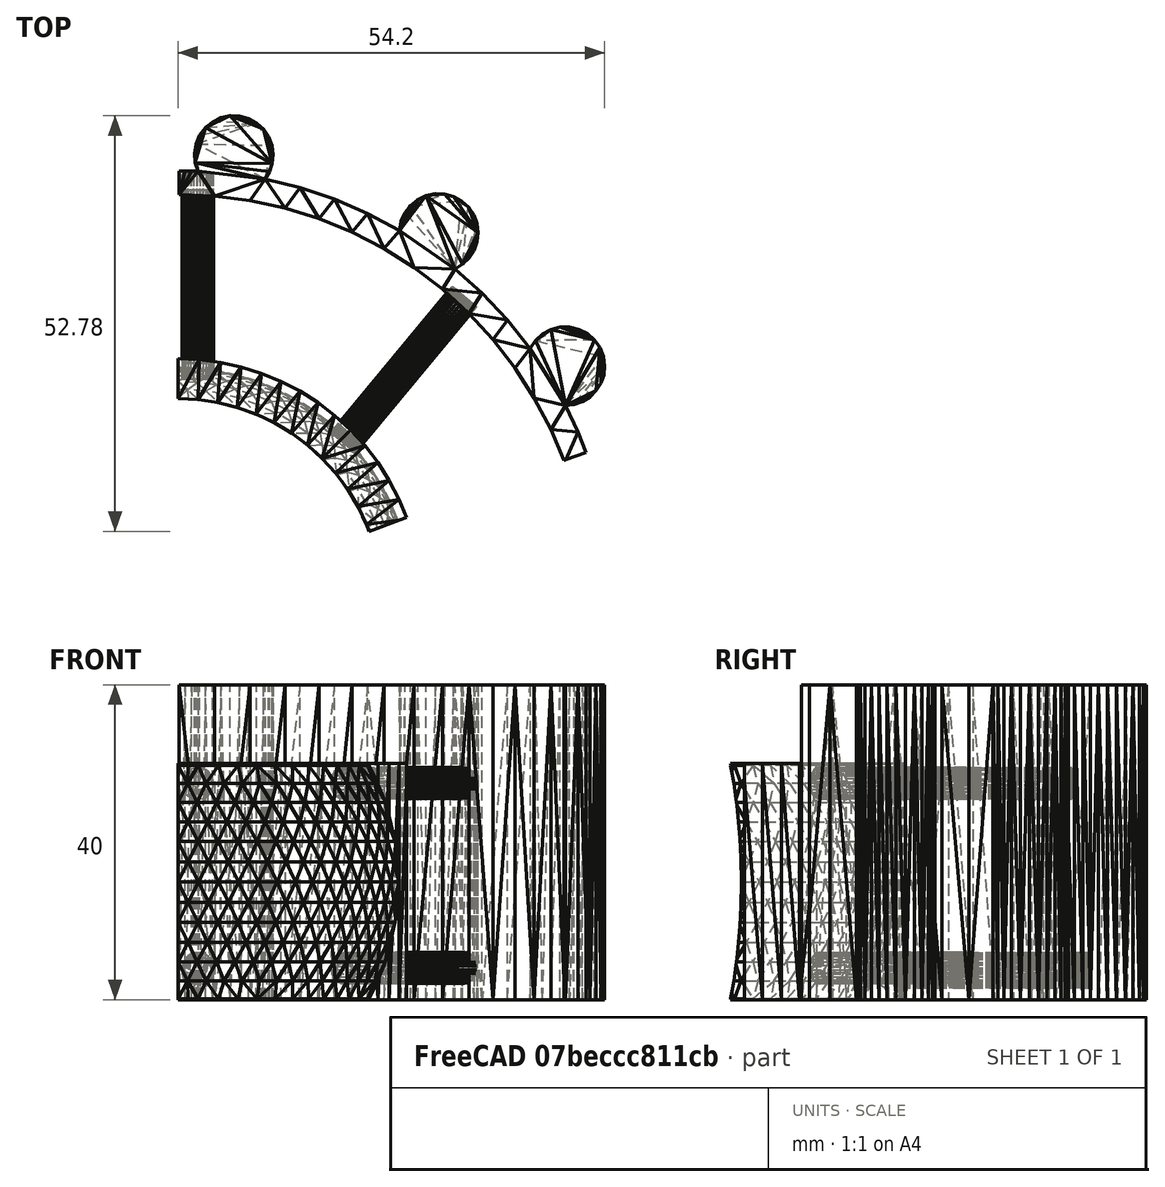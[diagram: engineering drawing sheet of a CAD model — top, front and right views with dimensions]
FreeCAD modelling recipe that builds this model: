
FCSTD DOCUMENT  (FreeCAD 1.1R43946 (Git))
Label: solid_door_handle_arthritis
License: All rights reserved
LicenseURL: https://en.wikipedia.org/wiki/All_rights_reserved
objects: Part::Box×3, Part::Cut×3, Mesh::Feature×1, Part::Feature×1
note: 7 computed .brp shape members not serialized (recipe doc carries the construction recipe); baked Part::Feature solids carry a one-line shape summary decoded from their .brp

FEATURE [Mesh::Feature] arthritis_door_handle_mk3
FEATURE [Part::Feature] arthritis_door_handle_mk001
  shape: bbox 64.29 x 63.81 x 40 mm, 1954 faces, 0 solids (baked)
FEATURE [Part::Box] Box  label="Cube"
  AttacherType = Attacher::AttachEngine3D
  Height = 100
  Length = 101
  Placement = pos=(0,-20,0) rot=(0,0,1;0.349066rad)
  Width = 19
FEATURE [Part::Cut] Cut
  Base = -> arthritis_door_handle_mk001
  Refine = true
  Tool = -> Box
FEATURE [Part::Box] Box001  label="Cube001"
  AttacherType = Attacher::AttachEngine3D
  Height = 45
  Length = 10
  Placement = pos=(-4,-3.5,0) rot=(0,0,1;0rad)
  Width = 10
FEATURE [Part::Cut] Cut001
  Base = -> Cut
  Refine = true
  Tool = -> Box001
FEATURE [Part::Box] Box002  label="Cube002"
  AttacherType = Attacher::AttachEngine3D
  Height = 62
  Length = 12
  Placement = pos=(50.5,-3.5,0) rot=(0,0,1;0rad)
  Width = 13
FEATURE [Part::Cut] Cut002
  Base = -> Cut001
  Refine = true
  Tool = -> Box002
